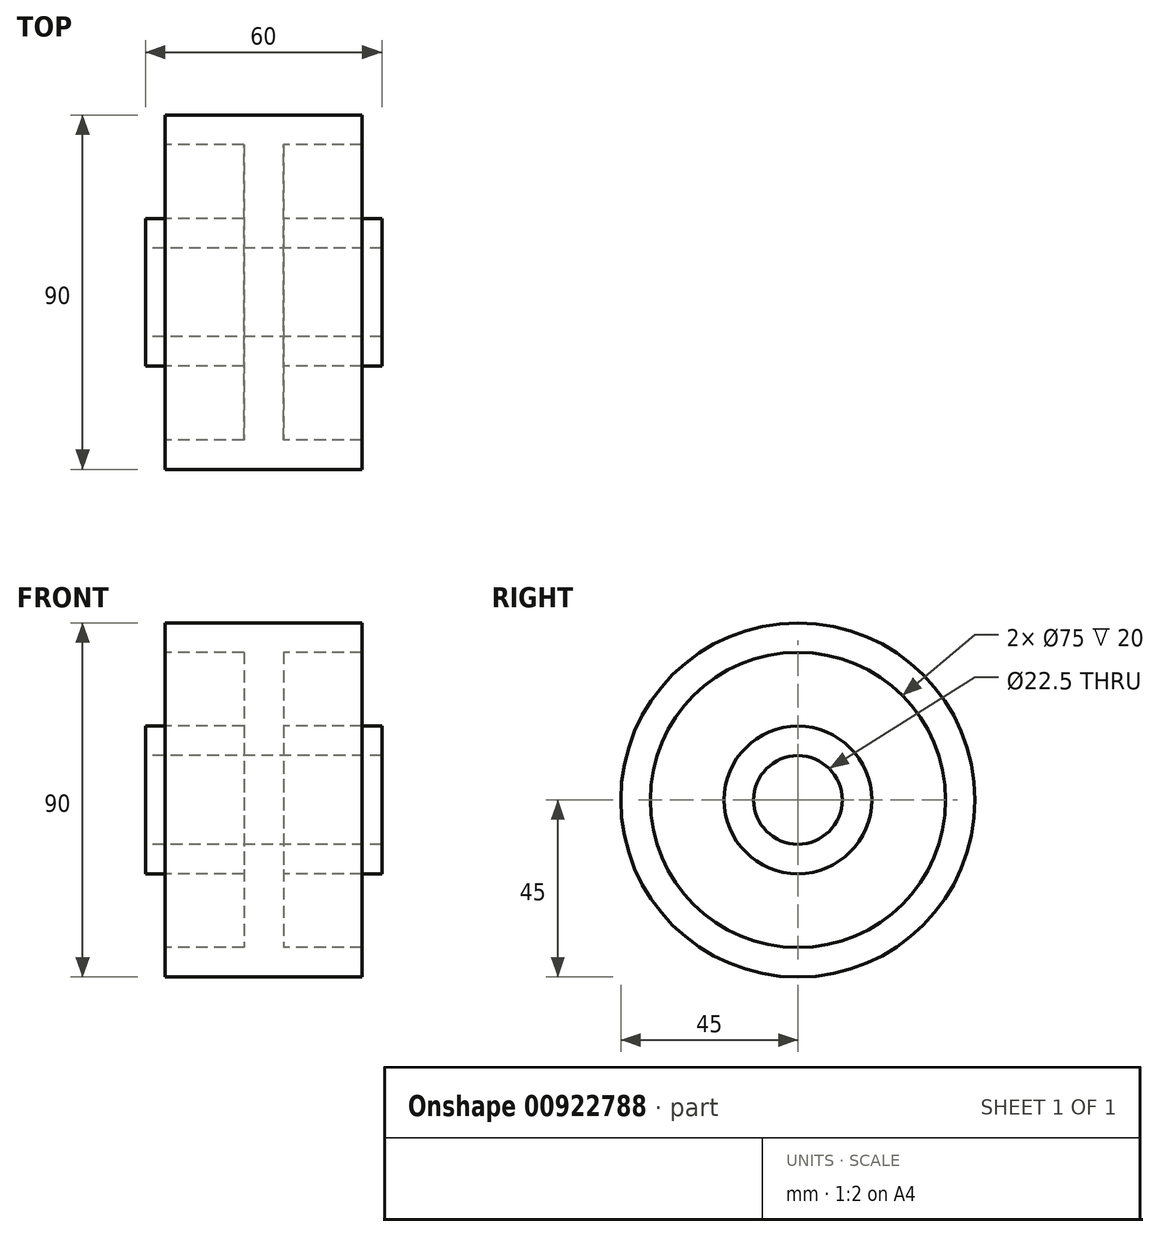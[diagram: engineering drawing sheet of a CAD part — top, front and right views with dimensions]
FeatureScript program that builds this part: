
annotation { "Feature Type Name" : "Feature", "Feature Type Description" : "" }
export const myFeature = defineFeature(function(context is Context, id is Id, definition is map)
    precondition{}
    {
        {
            var Q0;
            Q0=qCreatedBy(makeId("Front.planeOp"),FACE);
            var sketch = newSketch(context, id + "F0", { "sketchPlane" : qUnion([Q0])});
            skLineSegment(sketch, "E0", {"start": v(-64.24, 0) * mm, "end": v(62.97, 0) * mm, "construction": true});
            skLineSegment(sketch, "E1", {"start": v(-30, 11.25) * mm, "end": v(30, 11.25) * mm});
            skLineSegment(sketch, "E2", {"start": v(30, 11.25) * mm, "end": v(30, 18.75) * mm});
            skLineSegment(sketch, "E3", {"start": v(30, 18.75) * mm, "end": v(5, 18.75) * mm});
            skLineSegment(sketch, "E4", {"start": v(5, 18.75) * mm, "end": v(5, 37.5) * mm});
            skLineSegment(sketch, "E5", {"start": v(5, 37.5) * mm, "end": v(25, 37.5) * mm});
            skLineSegment(sketch, "E6", {"start": v(25, 37.5) * mm, "end": v(25, 45) * mm});
            skLineSegment(sketch, "E7", {"start": v(25, 45) * mm, "end": v(-25, 45) * mm});
            skLineSegment(sketch, "E8", {"start": v(-25, 45) * mm, "end": v(-25, 37.5) * mm});
            skLineSegment(sketch, "E9", {"start": v(-25, 37.5) * mm, "end": v(-5, 37.5) * mm});
            skLineSegment(sketch, "E10", {"start": v(-5, 37.5) * mm, "end": v(-5, 18.75) * mm});
            skLineSegment(sketch, "E11", {"start": v(-5, 18.75) * mm, "end": v(-30, 18.75) * mm});
            skLineSegment(sketch, "E12", {"start": v(-30, 18.75) * mm, "end": v(-30, 11.25) * mm});
            skLineSegment(sketch, "E13", {"start": v(0, 0) * mm, "end": v(0, 63.44) * mm, "construction": true});
            skSolve(sketch);
        }
        {
            var Q0;
            Q0 = qSketchRegion(id + "F0", true);
            var Q1;
            Q1=sQuery(id+"F0.wireOp",EDGE,"E0");
            revolve(context, id + "F1", {"surfaceOperationType" : NewSurfaceOperationType.NEW, "entities" : qUnion([Q0]), "axis" : qUnion([Q1]), "revolveType" : RevolveType.FULL});
        }
    });
